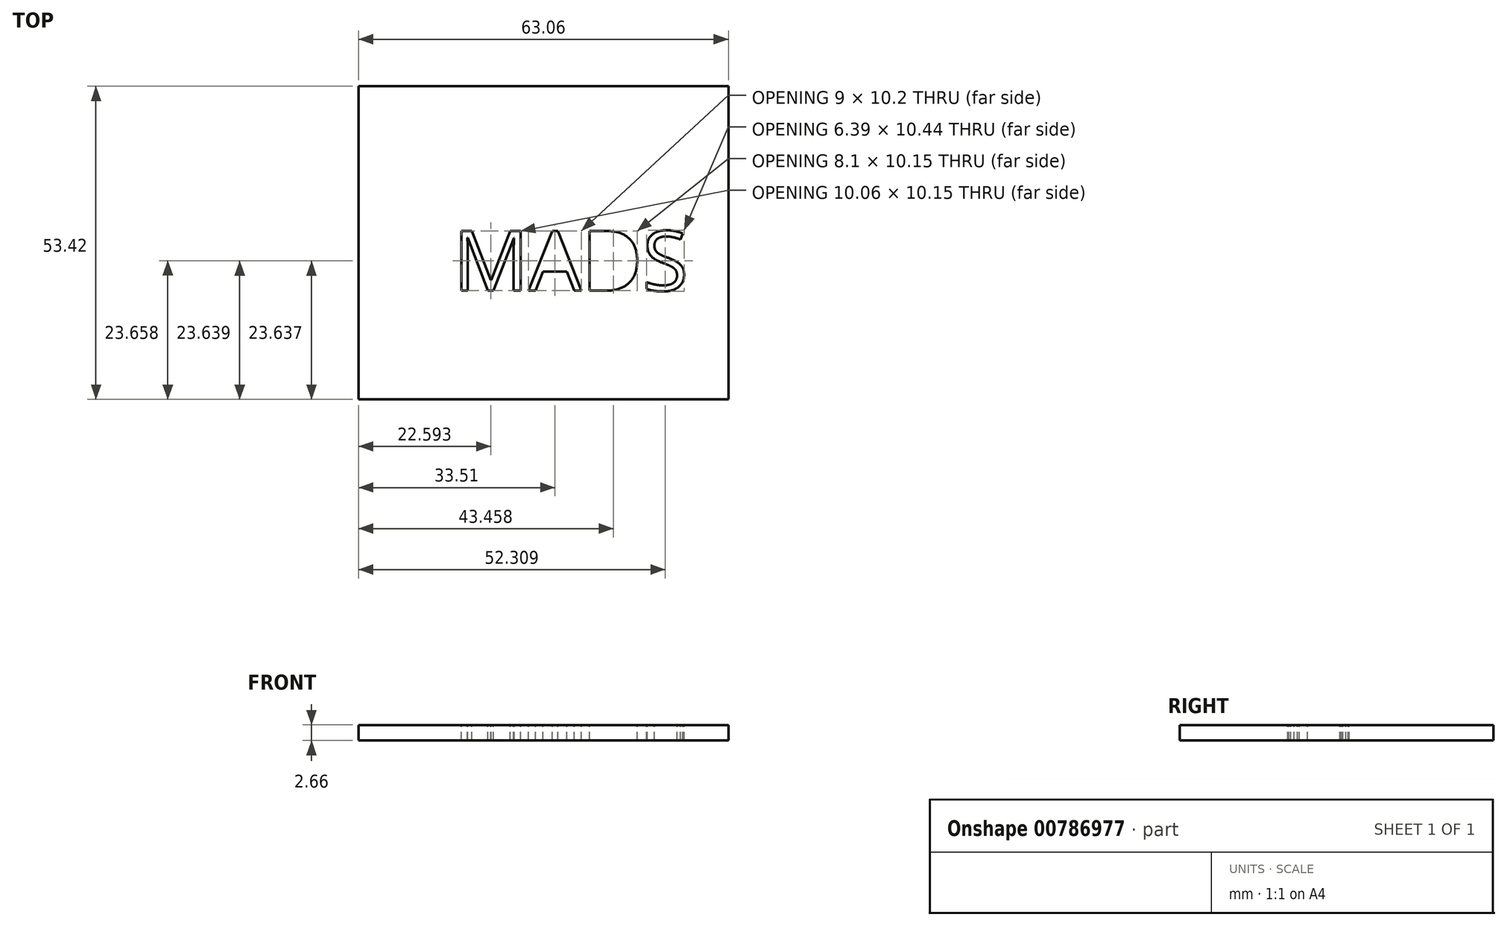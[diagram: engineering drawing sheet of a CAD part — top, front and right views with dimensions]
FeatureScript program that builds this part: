
annotation { "Feature Type Name" : "Feature", "Feature Type Description" : "" }
export const myFeature = defineFeature(function(context is Context, id is Id, definition is map)
    precondition{}
    {
        {
            var Q0;
            Q0=qCreatedBy(makeId("Top.planeOp"),FACE);
            var sketch = newSketch(context, id + "F0", { "sketchPlane" : qUnion([Q0])});
            skLineSegment(sketch, "E0.bottom", {"start": v(10.8, 66.64) * mm, "end": v(73.86, 66.64) * mm});
            skLineSegment(sketch, "E0.top", {"start": v(10.8, 13.22) * mm, "end": v(73.86, 13.22) * mm});
            skLineSegment(sketch, "E0.left", {"start": v(10.8, 66.64) * mm, "end": v(10.8, 13.22) * mm});
            skLineSegment(sketch, "E0.right", {"start": v(73.86, 66.64) * mm, "end": v(73.86, 13.22) * mm});
            skSolve(sketch);
        }
        {
            var Q0;
            Q0=makeQuery(id+"F0.imprint","IMPRINT",FACE,{"disambiguationData":[TD([[makeQuery(id+"F0.imprint","IMPRINT",EDGE,{"derivedFrom":sQuery(id+"F0.wireOp",EDGE,"E0.bottom")}),-1.0]])]});
            extrude(context, id + "F1", {"entities" : qUnion([Q0]), "depth" : 0 * yard, "offsetDistance" : 0.03 * yard});
        }
        {
            var Q0;
            Q0=makeQuery(id+"F1.opExtrude","CAP_FACE",FACE,{"disambiguationData":[OSD([sQuery(id+"F0.wireOp",EDGE,"E0.bottom"),sQuery(id+"F0.wireOp",EDGE,"E0.top"),sQuery(id+"F0.wireOp",EDGE,"E0.left"),sQuery(id+"F0.wireOp",EDGE,"E0.right")])],"isStart":false});
            var sketch = newSketch(context, id + "F2", { "sketchPlane" : qUnion([Q0])});
            skText(sketch, "E1", { "text": "MADS", "fontName": "OpenSans-Regular.ttf"});
            const initialGuessF2  = {"E1": [0.02697, 0.03178, 1, 0, 0.01024]};
            skSetInitialGuess(sketch, initialGuessF2);
            skSolve(sketch);
        }
        {
            var Q0;
            Q0=makeQuery(id+"F2.imprint","IMPRINT",FACE,{"disambiguationData":[TD([[makeQuery(id+"F2.imprint","IMPRINT",EDGE,{"derivedFrom":sQuery(id+"F2.wireOp",EDGE,"E1.sketch_text.stroke-0")}),1.0]])]});
            extrude(context, id + "F3", {"entities" : qUnion([Q0]), "operationType" : NewBodyOperationType.INTERSECT, "oppositeDirection" : true, "depth" : 0.03 * yard, "offsetDistance" : 0.03 * yard});
        }
    });
